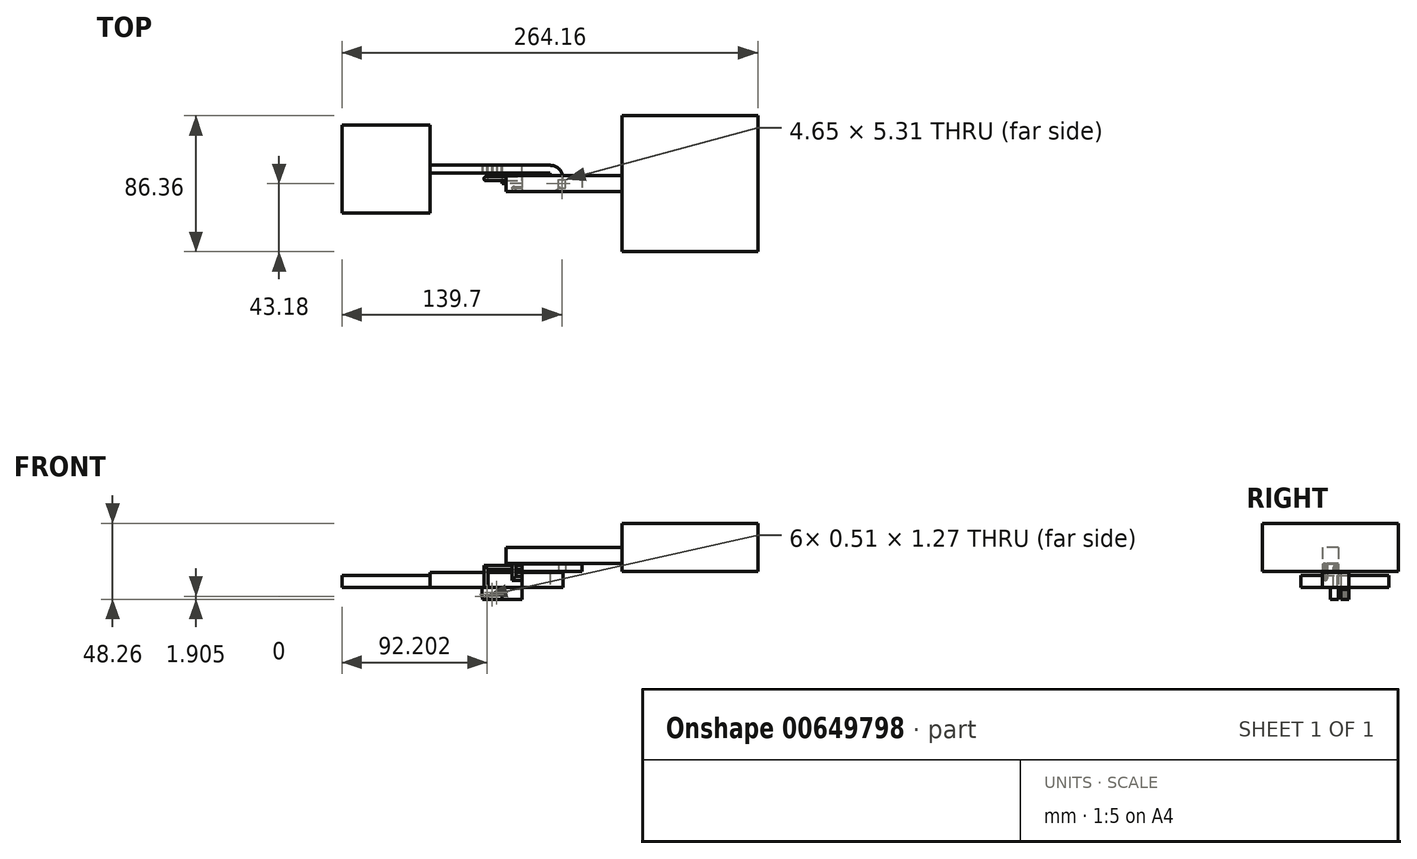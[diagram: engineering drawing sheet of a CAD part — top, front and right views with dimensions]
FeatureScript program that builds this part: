
annotation { "Feature Type Name" : "Feature", "Feature Type Description" : "" }
export const myFeature = defineFeature(function(context is Context, id is Id, definition is map)
    precondition{}
    {
        {
            var Q0;
            Q0=qCreatedBy(makeId("Top.planeOp"),FACE);
            var sketch = newSketch(context, id + "F0", { "sketchPlane" : qUnion([Q0])});
            skLineSegment(sketch, "E0.bottom", {"start": v(0, 0) * mm, "end": v(-25.4, 0) * mm});
            skLineSegment(sketch, "E0.top", {"start": v(0, -5.08) * mm, "end": v(-25.4, -5.08) * mm});
            skLineSegment(sketch, "E0.left", {"start": v(0, 0) * mm, "end": v(0, -5.08) * mm});
            skLineSegment(sketch, "E0.right", {"start": v(-25.4, 0) * mm, "end": v(-25.4, -5.08) * mm});
            skLineSegment(sketch, "E1.bottom", {"start": v(0, 0) * mm, "end": v(-6.35, 0) * mm});
            skLineSegment(sketch, "E1.top", {"start": v(0, 1.52) * mm, "end": v(-6.35, 1.52) * mm});
            skLineSegment(sketch, "E1.left", {"start": v(0, 0) * mm, "end": v(0, 1.52) * mm});
            skLineSegment(sketch, "E1.right", {"start": v(-6.35, 0) * mm, "end": v(-6.35, 1.52) * mm});
            skLineSegment(sketch, "E2.bottom", {"start": v(0, 1.52) * mm, "end": v(-25.4, 1.52) * mm});
            skLineSegment(sketch, "E2.top", {"start": v(0, 6.6) * mm, "end": v(-25.4, 6.6) * mm});
            skLineSegment(sketch, "E2.left", {"start": v(0, 1.52) * mm, "end": v(0, 6.6) * mm});
            skLineSegment(sketch, "E2.right", {"start": v(-25.4, 1.52) * mm, "end": v(-25.4, 6.6) * mm});
            skLineSegment(sketch, "E3", {"start": v(-12.7, 6.6) * mm, "end": v(-12.7, 1.52) * mm});
            skLineSegment(sketch, "E4", {"start": v(-12.7, 0) * mm, "end": v(-12.7, -5.08) * mm});
            skSolve(sketch);
        }
        {
            var Q0;
            Q0=qCreatedBy(makeId("Top.planeOp"),FACE);
            cPlane(context, id + "F1", {"entities" : qUnion([Q0]), "cplaneType" : CPlaneType.OFFSET, "offset" : 7.62 * mm, "width" : 152.4 * mm, "height" : 152.4 * mm});
        }
        {
            var Q0;
            Q0=qCreatedBy(id+"F1.planeOp",FACE);
            var sketch = newSketch(context, id + "F2", { "sketchPlane" : qUnion([Q0])});
            skLineSegment(sketch, "E5.bottom", {"start": v(0, 0) * mm, "end": v(17.78, 0) * mm});
            skLineSegment(sketch, "E5.left", {"start": v(0, 0) * mm, "end": v(0, -5.08) * mm});
            skLineSegment(sketch, "E5.right", {"start": v(17.78, 0) * mm, "end": v(17.78, -5.08) * mm});
            skLineSegment(sketch, "E6.bottom", {"start": v(17.78, 1.52) * mm, "end": v(-58.42, 1.52) * mm});
            skLineSegment(sketch, "E6.top", {"start": v(17.78, 6.6) * mm, "end": v(-58.42, 6.6) * mm});
            skLineSegment(sketch, "E6.left", {"start": v(17.78, 1.52) * mm, "end": v(17.78, 6.6) * mm});
            skLineSegment(sketch, "E6.right", {"start": v(-58.42, 1.52) * mm, "end": v(-58.42, 6.6) * mm});
            skLineSegment(sketch, "E7", {"start": v(17.78, 0) * mm, "end": v(17.78, 1.52) * mm});
            skLineSegment(sketch, "E8", {"start": v(0, -5.08) * mm, "end": v(0, -10.16) * mm});
            skLineSegment(sketch, "E9", {"start": v(0, -10.16) * mm, "end": v(17.78, -10.16) * mm});
            skLineSegment(sketch, "E10", {"start": v(17.78, -10.16) * mm, "end": v(17.78, -5.08) * mm});
            skArc(sketch, "E11", {"start": v(17.78, -10.16) * mm, "mid": v(26.16, -1.78) * mm, "end": v(17.78, 6.6) * mm});
            skCircle(sketch, "E12", {"center": v(-22.86, -1.9) * mm, "radius": 1.27 * mm});
            skSolve(sketch);
        }
        {
            var Q0;
            Q0=makeQuery(id+"F2.imprint","IMPRINT",FACE,{"disambiguationData":[TD([[makeQuery(id+"F2.imprint","IMPRINT",EDGE,{"derivedFrom":sQuery(id+"F2.wireOp",EDGE,"E6.bottom")}),-1.0]])]});
            var Q1;
            Q1=makeQuery(id+"F2.imprint","IMPRINT",FACE,{"disambiguationData":[TD([[makeQuery(id+"F2.imprint","IMPRINT",EDGE,{"derivedFrom":sQuery(id+"F2.wireOp",EDGE,"E5.bottom")}),-1.0]])]});
            var Q2;
            Q2=makeQuery(id+"F2.imprint","IMPRINT",FACE,{"disambiguationData":[TD([[makeQuery(id+"F2.imprint","IMPRINT",EDGE,{"derivedFrom":sQuery(id+"F2.wireOp",EDGE,"E5.right")}),1.0]])]});
            extrude(context, id + "F3", {"entities" : qUnion([Q0, Q1, Q2]), "depth" : 9.4 * mm, "offsetDistance" : 25.4 * mm});
        }
        {
            var Q0;
            Q0=qCreatedBy(makeId("Top.planeOp"),FACE);
            cPlane(context, id + "F4", {"entities" : qUnion([Q0]), "cplaneType" : CPlaneType.OFFSET, "offset" : 17.78 * mm, "width" : 152.4 * mm, "height" : 152.4 * mm});
        }
        {
            var Q0;
            Q0=qCreatedBy(id+"F4.planeOp",FACE);
            var sketch = newSketch(context, id + "F5", { "sketchPlane" : qUnion([Q0])});
            skLineSegment(sketch, "E13.bottom", {"start": v(0, 0) * mm, "end": v(38.1, 0) * mm});
            skLineSegment(sketch, "E13.top", {"start": v(0, -10.16) * mm, "end": v(38.1, -10.16) * mm});
            skLineSegment(sketch, "E13.left", {"start": v(0, 0) * mm, "end": v(0, -10.16) * mm});
            skLineSegment(sketch, "E13.right", {"start": v(38.1, 0) * mm, "end": v(38.1, -10.16) * mm});
            skPoint(sketch, "E14.middle", {"position": v(19.05, -5.08) * mm});
            skPoint(sketch, "E14.middle.positionSnap0", {"position": v(38.1, -5.08) * mm});
            skPoint(sketch, "E14.middle.positionSnap1", {"position": v(19.05, 0) * mm});
            skPoint(sketch, "E14.centerSnap0", {"position": v(38.1, -5.08) * mm});
            skPoint(sketch, "E14.centerSnap1", {"position": v(19.05, 0) * mm});
            skLineSegment(sketch, "E15.bottom", {"start": v(23.07, -7.74) * mm, "end": v(27.73, -7.74) * mm});
            skLineSegment(sketch, "E15.top", {"start": v(23.07, -2.42) * mm, "end": v(27.73, -2.42) * mm});
            skLineSegment(sketch, "E15.left", {"start": v(23.07, -7.74) * mm, "end": v(23.07, -2.42) * mm});
            skLineSegment(sketch, "E15.right", {"start": v(27.73, -7.74) * mm, "end": v(27.73, -2.42) * mm});
            skPoint(sketch, "E15.middle", {"position": v(25.4, -5.08) * mm});
            skSolve(sketch);
        }
        {
            var Q0;
            Q0=qCreatedBy(makeId("Top.planeOp"),FACE);
            cPlane(context, id + "F6", {"entities" : qUnion([Q0]), "cplaneType" : CPlaneType.OFFSET, "offset" : 22.86 * mm, "width" : 152.4 * mm, "height" : 152.4 * mm});
        }
        {
            var Q0;
            Q0=qCreatedBy(id+"F6.planeOp",FACE);
            var sketch = newSketch(context, id + "F7", { "sketchPlane" : qUnion([Q0])});
            skLineSegment(sketch, "E16.bottom", {"start": v(0, 0) * mm, "end": v(-10.16, 0) * mm});
            skLineSegment(sketch, "E16.top", {"start": v(0, -10.16) * mm, "end": v(-10.16, -10.16) * mm});
            skLineSegment(sketch, "E16.left", {"start": v(0, 0) * mm, "end": v(0, -10.16) * mm});
            skLineSegment(sketch, "E16.right", {"start": v(-10.16, 0) * mm, "end": v(-10.16, -10.16) * mm});
            skLineSegment(sketch, "E17.bottom", {"start": v(0, 0) * mm, "end": v(63.5, 0) * mm});
            skLineSegment(sketch, "E17.top", {"start": v(0, -10.16) * mm, "end": v(63.5, -10.16) * mm});
            skLineSegment(sketch, "E17.right", {"start": v(63.5, 0) * mm, "end": v(63.5, -10.16) * mm});
            skCircle(sketch, "E18", {"center": v(-5.08, -8.26) * mm, "radius": 1.27 * mm});
            skSolve(sketch);
        }
        {
            var Q0;
            Q0=qCreatedBy(makeId("Right.planeOp"),FACE);
            var sketch = newSketch(context, id + "F8", { "sketchPlane" : qUnion([Q0])});
            skCircle(sketch, "E19", {"center": v(-8.33, 13.34) * mm, "radius": 1.27 * mm});
            skCircle(sketch, "E20", {"center": v(-1.9, 20.32) * mm, "radius": 1.27 * mm});
            skSolve(sketch);
        }
        {
            var Q0;
            Q0=qCreatedBy(makeId("Front.planeOp"),FACE);
            cPlane(context, id + "F9", {"entities" : qUnion([Q0]), "cplaneType" : CPlaneType.OFFSET, "offset" : 8.25 * mm, "width" : 152.4 * mm, "height" : 152.4 * mm});
        }
        {
            var Q0;
            Q0=qCreatedBy(id+"F9.planeOp",FACE);
            var sketch = newSketch(context, id + "F10", { "sketchPlane" : qUnion([Q0])});
            skLineSegment(sketch, "E21", {"start": v(0, 13.34) * mm, "end": v(-5.08, 13.34) * mm});
            skLineSegment(sketch, "E22", {"start": v(-5.08, 13.34) * mm, "end": v(-5.08, 22.86) * mm});
            skSolve(sketch);
        }
        {
            var Q0;
            Q0=makeQuery(id+"F5.imprint","IMPRINT",FACE,{"disambiguationData":[TD([[makeQuery(id+"F5.imprint","IMPRINT",EDGE,{"derivedFrom":sQuery(id+"F5.wireOp",EDGE,"E13.bottom")}),-1.0]])]});
            extrude(context, id + "F11", {"entities" : qUnion([Q0]), "depth" : 4.57 * mm, "offsetDistance" : 25.4 * mm});
        }
        {
            var Q0;
            Q0=makeQuery(id+"F7.imprint","IMPRINT",FACE,{"disambiguationData":[TD([[makeQuery(id+"F7.imprint","IMPRINT",EDGE,{"derivedFrom":sQuery(id+"F7.wireOp",EDGE,"E16.bottom")}),1.0]])]});
            var Q1;
            Q1=makeQuery(id+"F7.imprint","IMPRINT",FACE,{"disambiguationData":[TD([[makeQuery(id+"F7.imprint","IMPRINT",EDGE,{"derivedFrom":sQuery(id+"F7.wireOp",EDGE,"E17.bottom")}),-1.0]])]});
            var Q2;
            Q2=makeQuery(id+"F7.imprint","IMPRINT",FACE,{"disambiguationData":[TD([[makeQuery(id+"F7.imprint","IMPRINT",EDGE,{"derivedFrom":sQuery(id+"F7.wireOp",EDGE,"E18")}),1.0]])]});
            extrude(context, id + "F12", {"entities" : qUnion([Q0, Q1, Q2]), "operationType" : NewBodyOperationType.ADD, "depth" : 10.16 * mm, "offsetDistance" : 25.4 * mm});
        }
        {
            var Q0;
            Q0=qCreatedBy(makeId("Front.planeOp"),FACE);
            cPlane(context, id + "F13", {"entities" : qUnion([Q0]), "cplaneType" : CPlaneType.OFFSET, "offset" : 1.9 * mm, "width" : 152.4 * mm, "height" : 152.4 * mm});
        }
        {
            var Q0;
            Q0=qCreatedBy(id+"F13.planeOp",FACE);
            var sketch = newSketch(context, id + "F14", { "sketchPlane" : qUnion([Q0])});
            skLineSegment(sketch, "E23", {"start": v(0, 20.32) * mm, "end": v(-22.86, 20.32) * mm});
            skLineSegment(sketch, "E24", {"start": v(-22.86, 7.62) * mm, "end": v(-22.86, 20.32) * mm});
            skSolve(sketch);
        }
        {
            var Q0;
            Q0=makeQuery(id+"F8.imprint","IMPRINT",FACE,{"disambiguationData":[TD([[makeQuery(id+"F8.imprint","IMPRINT",EDGE,{"derivedFrom":sQuery(id+"F8.wireOp",EDGE,"E20")}),1.0]])]});
            var Q1;
            Q1=makeQuery(id+"F2.imprint","IMPRINT",FACE,{"disambiguationData":[TD([[makeQuery(id+"F2.imprint","IMPRINT",EDGE,{"derivedFrom":sQuery(id+"F2.wireOp",EDGE,"E12")}),1.0]])]});
            var Q2;
            Q2=sQuery(id+"F14.wireOp",EDGE,"E23");
            var Q3;
            Q3=sQuery(id+"F14.wireOp",EDGE,"E24");
            sweep(context, id + "F15", {"operationType" : NewBodyOperationType.ADD, "profiles" : qUnion([Q0, Q1]), "path" : qUnion([Q2, Q3])});
        }
        {
            var Q0;
            Q0=qCreatedBy(makeId("Front.planeOp"),FACE);
            cPlane(context, id + "F16", {"entities" : qUnion([Q0]), "cplaneType" : CPlaneType.OFFSET, "offset" : 4.06 * mm, "oppositeDirection" : true, "width" : 152.4 * mm, "height" : 152.4 * mm});
        }
        {
            var Q0;
            Q0=qCreatedBy(id+"F16.planeOp",FACE);
            var sketch = newSketch(context, id + "F17", { "sketchPlane" : qUnion([Q0])});
            skLineSegment(sketch, "E25.bottom", {"start": v(-12.7, 6.6) * mm, "end": v(-13.2, 6.6) * mm});
            skLineSegment(sketch, "E25.top", {"start": v(-12.7, 5.08) * mm, "end": v(-13.2, 5.08) * mm});
            skLineSegment(sketch, "E25.left", {"start": v(-12.7, 6.6) * mm, "end": v(-12.7, 5.08) * mm});
            skLineSegment(sketch, "E25.right", {"start": v(-13.2, 6.6) * mm, "end": v(-13.2, 5.08) * mm});
            skLineSegment(sketch, "E26.bottom", {"start": v(-25.4, 0) * mm, "end": v(-24.9, 0) * mm});
            skLineSegment(sketch, "E26.top", {"start": v(-25.4, 1.27) * mm, "end": v(-24.9, 1.27) * mm});
            skLineSegment(sketch, "E26.left", {"start": v(-25.4, 0) * mm, "end": v(-25.4, 1.27) * mm});
            skLineSegment(sketch, "E26.right", {"start": v(-24.9, 0) * mm, "end": v(-24.9, 1.27) * mm});
            skLineSegment(sketch, "E27.bottom", {"start": v(-18.8, 3.81) * mm, "end": v(-19.3, 3.81) * mm});
            skLineSegment(sketch, "E27.top", {"start": v(-18.8, 2.54) * mm, "end": v(-19.3, 2.54) * mm});
            skLineSegment(sketch, "E27.left", {"start": v(-18.8, 3.81) * mm, "end": v(-18.8, 2.54) * mm});
            skLineSegment(sketch, "E27.right", {"start": v(-19.3, 3.81) * mm, "end": v(-19.3, 2.54) * mm});
            skPoint(sketch, "E27.middle", {"position": v(-19.05, 3.17) * mm});
            skLineSegment(sketch, "E28.bottom", {"start": v(-15.75, 5.08) * mm, "end": v(-16.26, 5.08) * mm});
            skLineSegment(sketch, "E28.top", {"start": v(-15.75, 3.8) * mm, "end": v(-16.26, 3.8) * mm});
            skLineSegment(sketch, "E28.left", {"start": v(-15.75, 5.08) * mm, "end": v(-15.75, 3.8) * mm});
            skLineSegment(sketch, "E28.right", {"start": v(-16.26, 5.08) * mm, "end": v(-16.26, 3.8) * mm});
            skPoint(sketch, "E28.middle", {"position": v(-16, 4.45) * mm});
            skLineSegment(sketch, "E29.bottom", {"start": v(-21.84, 2.54) * mm, "end": v(-22.35, 2.54) * mm});
            skLineSegment(sketch, "E29.top", {"start": v(-21.84, 1.27) * mm, "end": v(-22.35, 1.27) * mm});
            skLineSegment(sketch, "E29.left", {"start": v(-21.84, 2.54) * mm, "end": v(-21.84, 1.27) * mm});
            skLineSegment(sketch, "E29.right", {"start": v(-22.35, 2.54) * mm, "end": v(-22.35, 1.27) * mm});
            skPoint(sketch, "E29.middle", {"position": v(-22.1, 1.9) * mm});
            skSolve(sketch);
        }
        {
            var Q0;
            Q0=makeQuery(id+"F8.imprint","IMPRINT",FACE,{"disambiguationData":[TD([[makeQuery(id+"F8.imprint","IMPRINT",EDGE,{"derivedFrom":sQuery(id+"F8.wireOp",EDGE,"E19")}),1.0]])]});
            var Q1;
            Q1=makeQuery(id+"F7.imprint","IMPRINT",FACE,{"disambiguationData":[TD([[makeQuery(id+"F7.imprint","IMPRINT",EDGE,{"derivedFrom":sQuery(id+"F7.wireOp",EDGE,"E18")}),1.0]])]});
            var Q2;
            Q2=sQuery(id+"F10.wireOp",EDGE,"E22");
            var Q3;
            Q3=sQuery(id+"F10.wireOp",EDGE,"E21");
            sweep(context, id + "F18", {"operationType" : NewBodyOperationType.ADD, "profiles" : qUnion([Q0, Q1]), "path" : qUnion([Q2, Q3])});
        }
        {
            var Q0;
            Q0=makeQuery(id+"F0.imprint","IMPRINT",FACE,{"disambiguationData":[TD([[makeQuery(id+"F0.imprint","IMPRINT",EDGE,{"derivedFrom":sQuery(id+"F0.wireOp",EDGE,"E0.bottom")}),1.0]])]});
            extrude(context, id + "F19", {"entities" : qUnion([Q0]), "depth" : 7.62 * mm, "offsetDistance" : 25.4 * mm});
        }
        {
            var Q0;
            {var subQ2=sQuery(id+"F0.wireOp",EDGE,"E0.left");Q0=makeQuery(id+"F0.imprint","IMPRINT",FACE,{"disambiguationData":[TD([[makeQuery(id+"F0.imprint","IMPRINT",EDGE,{"derivedFrom":subQ2}),-1.0]])]});}
            extrude(context, id + "F20", {"entities" : qUnion([Q0]), "operationType" : NewBodyOperationType.ADD, "depth" : 7.11 * mm, "offsetDistance" : 25.4 * mm});
        }
        {
            var Q0;
            Q0=makeQuery(id+"F0.imprint","IMPRINT",FACE,{"disambiguationData":[TD([[makeQuery(id+"F0.imprint","IMPRINT",EDGE,{"derivedFrom":sQuery(id+"F0.wireOp",EDGE,"E1.bottom")}),-1.0]])]});
            var Q1;
            {var subQ0=sQuery(id+"F0.wireOp",EDGE,"E2.left");Q1=makeQuery(id+"F0.imprint","IMPRINT",FACE,{"disambiguationData":[TD([[makeQuery(id+"F0.imprint","IMPRINT",EDGE,{"derivedFrom":subQ0}),1.0]])]});}
            extrude(context, id + "F21", {"entities" : qUnion([Q0, Q1]), "operationType" : NewBodyOperationType.ADD, "depth" : 6.35 * mm, "offsetDistance" : 25.4 * mm});
        }
        {
            var Q0;
            {var subQ0=sQuery(id+"F0.wireOp",EDGE,"E2.right");Q0=makeQuery(id+"F0.imprint","IMPRINT",FACE,{"disambiguationData":[TD([[makeQuery(id+"F0.imprint","IMPRINT",EDGE,{"derivedFrom":subQ0}),-1.0]])]});}
            extrude(context, id + "F22", {"entities" : qUnion([Q0]), "depth" : 7.62 * mm, "offsetDistance" : 25.4 * mm});
        }
        {
            var Q0;
            Q0 = qSketchRegion(id + "F17", true);
            extrude(context, id + "F23", {"entities" : qUnion([Q0]), "operationType" : NewBodyOperationType.REMOVE, "endBound" : BoundingType.SYMMETRIC, "oppositeDirection" : true, "depth" : 5.08 * mm, "offsetDistance" : 25.4 * mm});
        }
        {
            var Q0;
            Q0=qCreatedBy(id+"F4.planeOp",FACE);
            var sketch = newSketch(context, id + "F24", { "sketchPlane" : qUnion([Q0])});
            skLineSegment(sketch, "E30.bottom", {"start": v(63.5, 38.1) * mm, "end": v(149.86, 38.1) * mm});
            skLineSegment(sketch, "E30.top", {"start": v(63.5, -48.26) * mm, "end": v(149.86, -48.26) * mm});
            skLineSegment(sketch, "E30.left", {"start": v(63.5, 38.1) * mm, "end": v(63.5, -48.26) * mm});
            skLineSegment(sketch, "E30.right", {"start": v(149.86, 38.1) * mm, "end": v(149.86, -48.26) * mm});
            skSolve(sketch);
        }
        {
            var Q0;
            Q0=makeQuery(id+"F24.imprint","IMPRINT",FACE,{"disambiguationData":[TD([[makeQuery(id+"F24.imprint","IMPRINT",EDGE,{"derivedFrom":sQuery(id+"F24.wireOp",EDGE,"E30.bottom")}),-1.0]])]});
            extrude(context, id + "F25", {"entities" : qUnion([Q0]), "operationType" : NewBodyOperationType.ADD, "depth" : 30.48 * mm, "offsetDistance" : 25.4 * mm});
        }
        {
            var Q0;
            Q0=qCreatedBy(id+"F1.planeOp",FACE);
            var sketch = newSketch(context, id + "F26", { "sketchPlane" : qUnion([Q0])});
            skLineSegment(sketch, "E31.bottom", {"start": v(-58.42, -23.88) * mm, "end": v(-114.3, -23.88) * mm});
            skLineSegment(sketch, "E31.top", {"start": v(-58.42, 32) * mm, "end": v(-114.3, 32) * mm});
            skLineSegment(sketch, "E31.left", {"start": v(-58.42, -23.88) * mm, "end": v(-58.42, 32) * mm});
            skLineSegment(sketch, "E31.right", {"start": v(-114.3, -23.88) * mm, "end": v(-114.3, 32) * mm});
            skSolve(sketch);
        }
        {
            var Q0;
            Q0=makeQuery(id+"F26.imprint","IMPRINT",FACE,{"disambiguationData":[TD([[makeQuery(id+"F26.imprint","IMPRINT",EDGE,{"derivedFrom":sQuery(id+"F26.wireOp",EDGE,"E31.bottom")}),-1.0]])]});
            extrude(context, id + "F27", {"entities" : qUnion([Q0]), "operationType" : NewBodyOperationType.ADD, "depth" : 7.62 * mm, "offsetDistance" : 25.4 * mm});
        }
        {
            var Q0;
            Q0=makeQuery(id+"F5.imprint","IMPRINT",FACE,{"disambiguationData":[TD([[makeQuery(id+"F5.imprint","IMPRINT",EDGE,{"derivedFrom":sQuery(id+"F5.wireOp",EDGE,"E15.bottom")}),1.0]])]});
            extrude(context, id + "F28", {"entities" : qUnion([Q0]), "depth" : 5.08 * mm, "offsetDistance" : 25.4 * mm});
        }
    });
